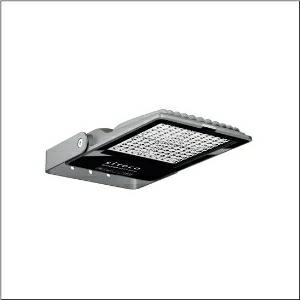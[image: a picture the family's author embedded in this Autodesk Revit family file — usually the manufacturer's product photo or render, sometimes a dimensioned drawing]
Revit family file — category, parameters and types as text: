
# Revit family: sicompact_31_mini___pl32_5xa7571f2k23_1d04
name_source: partatom
category: Lighting Fixtures
units: mm (PartAtom-declared; Revit-internal decimal feet)

## family parameters
Cut with Voids When Loaded = No
Host = Face
Light Source = No
Part Type = Normal
Room Calculation Point = No
Round Connector Dimension = Use Diameter
Shared = No

## types (1)
- SiCompact 31 mini  PL32 (1 x LED, 20000 lm, 130 W, 4000K)
    Apparent Load = 130 VA
    CIE Flux Codes = 32 69 98 100 100
    Color Rendering = 70
    Color Temperature = 4000K
    Default Elevation = 1800 mm
    Description = SiCompact 31 mini, floodlight, primary light control with lens, of plastic, of toughened safety glass, transparent, light distribution: PL32, light emission: direct distribution, primary light characteristic: asymmetric, installation type: surface-mounted, LED, High Power LED, rated luminous flux: 20.000lm, luminous efficacy: 154lm/W, light colour: 740, colour temperature: 4000K, control gear: ON/OFF, with cable, 3x 1.5mm², mains connection: 220..240V, AC, 50/60Hz, connection cable pre-assembled, cable length: 2m, rated input power: 130W, of diecast aluminium, specular, metallic grey (RAL 9006), length: 461mm, width: 261mm, height: 62mm, bracket, of sheet steel, coated, metallic grey (RAL 9006), ON/OFF, protection rating (complete): IP66, insulation class (complete): insulation class I (protective earthing), certification: CE, ENEC, impact resistance: IK08, permissible operating ambient temperature: -40..+45°C, packaging unit: 1 piece

Light Distribution: PL32
    Height = 62 mm  [stored 0.203412 ft]
    Lamp = 1 x LED
    Lamp Light Flux = 20000 lm
    Lamp Power = 130 W
    Lamp count = 1
    Length = 460 mm
    Luminous efficacy = 154 lm/W
    Manufacturer = Siteco
    ModVariant = No
    Model = 5XA7571F2K23
    Mounting Place = Wall
    Mounting Type = Surface mounted
    Number of Poles = 1
    OnlyDefault = Yes
    Power Factor = 1
    Product Name = SiCompact 31 mini | PL32
    Product group = floodlight | wall mounted
    ProductGroupID = 2002
    Protection Class = Protection class I
    Protection Degree = IP 66
    RLX_Detail_Level = 1
    RLX_Emergency_Light_Flux = 0 lm
    RLX_Emergency_Type = 0
    RLX_Emergency_Type_DB = No
    RlxData = <blob elided: 126689 chars, md5=fb1e56aa>
    Socket = socket
    Standby Power = 0 W
    System Light Flux = 20000 lm
    System Power = 130 W
    Type Comments = Product without accessories
    Type Image = l_1006951.jpg
    URL = http://relux.com
    VarID = ---
    Voltage = 0 V
    Weight = 0.00 kg
    Width = 260 mm

note: [stored X ft] marks values corroborated as IEEE doubles in the binary element streams (Revit-internal decimal feet)

## geometry (parser evidence)
native form markers: Blend x4, Sweep x14
no freeform markers — native parametric forms only
